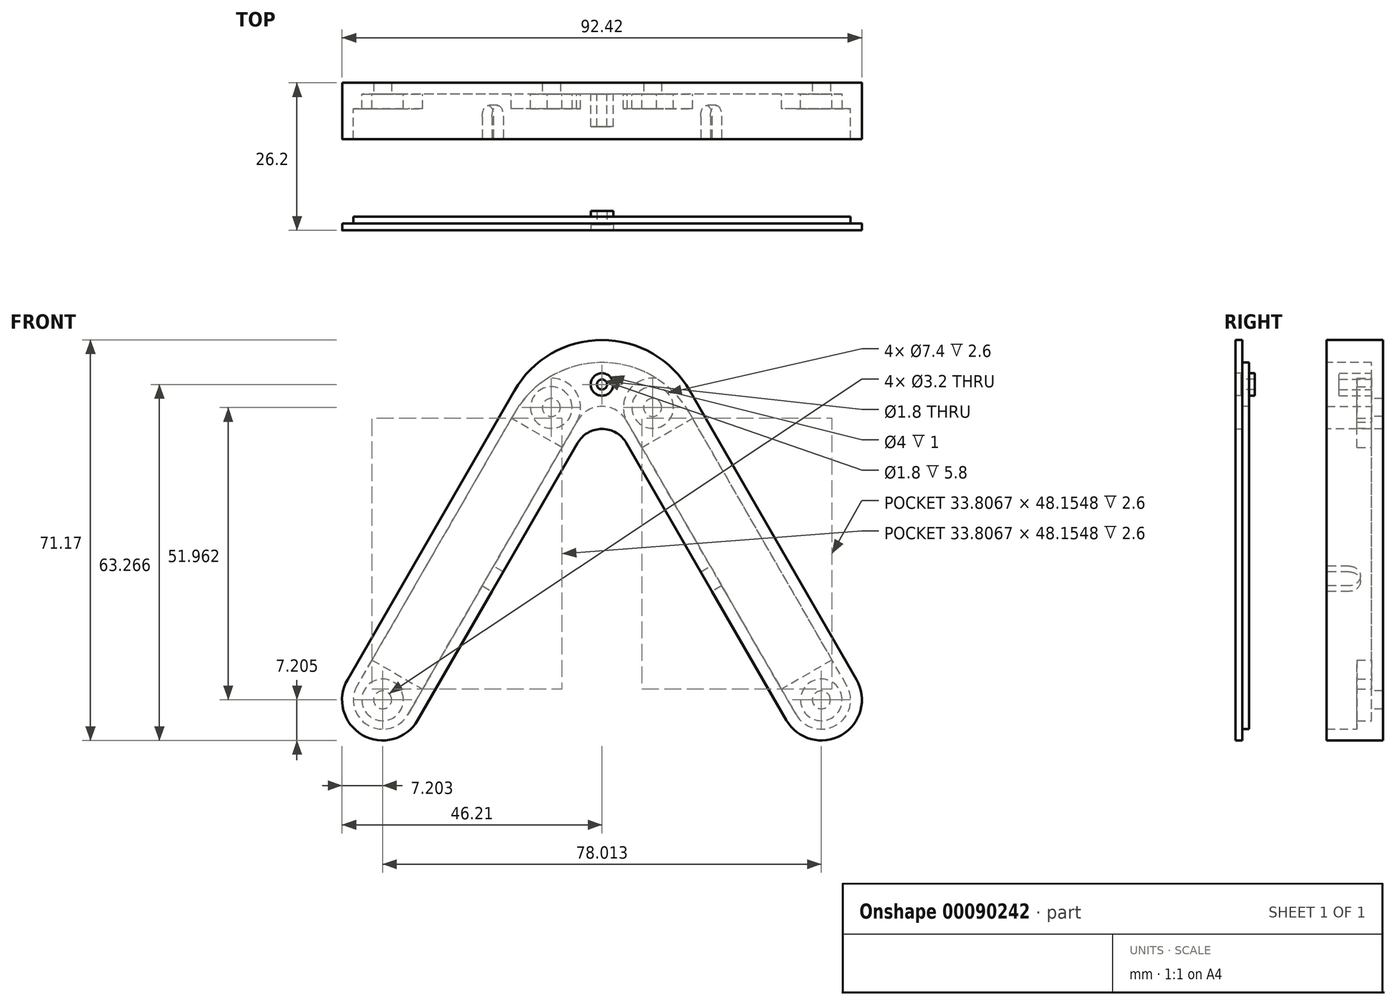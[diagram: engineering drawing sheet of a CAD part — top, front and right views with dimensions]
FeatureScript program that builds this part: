
annotation { "Feature Type Name" : "Feature", "Feature Type Description" : "" }
export const myFeature = defineFeature(function(context is Context, id is Id, definition is map)
    precondition{}
    {
        {
            var Q0;
            Q0=qCreatedBy(makeId("Front.planeOp"),FACE);
            var sketch = newSketch(context, id + "F0", { "sketchPlane" : qUnion([Q0])});
            skLineSegment(sketch, "E0", {"start": v(0, 45.47) * mm, "end": v(-52.5, -45.47) * mm});
            skLineSegment(sketch, "E1", {"start": v(-52.5, -45.47) * mm, "end": v(-35.87, -45.47) * mm});
            skLineSegment(sketch, "E2", {"start": v(52.5, -45.47) * mm, "end": v(0, 45.47) * mm});
            skLineSegment(sketch, "E3.0", {"start": v(35.87, -45.47) * mm, "end": v(0, 16.67) * mm});
            skLineSegment(sketch, "E3.2", {"start": v(0, 16.67) * mm, "end": v(-35.87, -45.47) * mm});
            skLineSegment(sketch, "E4.trimOffspring", {"start": v(35.87, -45.47) * mm, "end": v(52.5, -45.47) * mm});
            skSolve(sketch);
        }
        {
            var Q0;
            Q0 = qSketchRegion(id + "F0", true);
            extrude(context, id + "F1", {"entities" : qUnion([Q0]), "depth" : 2 * mm});
        }
        {
            var Q0;
            Q0=makeQuery(id+"F1.opExtrude","CAP_FACE",FACE,{"disambiguationData":[OSD([sQuery(id+"F0.wireOp",EDGE,"E0"),sQuery(id+"F0.wireOp",EDGE,"E1"),sQuery(id+"F0.wireOp",EDGE,"E2"),sQuery(id+"F0.wireOp",EDGE,"E3.0"),sQuery(id+"F0.wireOp",EDGE,"E3.2"),sQuery(id+"F0.wireOp",EDGE,"E4.trimOffspring")])],"isStart":false});
            var sketch = newSketch(context, id + "F2", { "sketchPlane" : qUnion([Q0])});
            skLineSegment(sketch, "E5.0", {"start": v(0, 16.67) * mm, "end": v(-35.87, -45.47) * mm});
            skLineSegment(sketch, "E5.1", {"start": v(0, 45.47) * mm, "end": v(-52.5, -45.47) * mm});
            skLineSegment(sketch, "E5.2", {"start": v(-52.5, -45.47) * mm, "end": v(-35.87, -45.47) * mm});
            skLineSegment(sketch, "E5.3", {"start": v(35.87, -45.47) * mm, "end": v(0, 16.67) * mm});
            skLineSegment(sketch, "E5.4", {"start": v(35.87, -45.47) * mm, "end": v(52.5, -45.47) * mm});
            skLineSegment(sketch, "E5.5", {"start": v(52.5, -45.47) * mm, "end": v(0, 45.47) * mm});
            skLineSegment(sketch, "E6.0", {"start": v(37.03, -43.47) * mm, "end": v(0, 20.67) * mm});
            skLineSegment(sketch, "E6.1", {"start": v(-49.04, -43.47) * mm, "end": v(-37.03, -43.47) * mm});
            skLineSegment(sketch, "E6.2", {"start": v(0, 41.47) * mm, "end": v(-49.04, -43.47) * mm});
            skLineSegment(sketch, "E6.3", {"start": v(0, 20.67) * mm, "end": v(-37.03, -43.47) * mm});
            skLineSegment(sketch, "E6.4", {"start": v(49.04, -43.47) * mm, "end": v(0, 41.47) * mm});
            skLineSegment(sketch, "E6.5", {"start": v(37.03, -43.47) * mm, "end": v(49.04, -43.47) * mm});
            skSolve(sketch);
        }
        {
            var Q0;
            Q0 = qSketchRegion(id + "F2", true);
            extrude(context, id + "F3", {"entities" : qUnion([Q0]), "operationType" : NewBodyOperationType.ADD, "depth" : 8 * mm});
        }
        {
            var Q0;
            Q0=makeQuery(id+"F1.opExtrude","CAP_FACE",FACE,{"disambiguationData":[OSD([sQuery(id+"F0.wireOp",EDGE,"E0"),sQuery(id+"F0.wireOp",EDGE,"E1"),sQuery(id+"F0.wireOp",EDGE,"E2"),sQuery(id+"F0.wireOp",EDGE,"E3.0"),sQuery(id+"F0.wireOp",EDGE,"E3.2"),sQuery(id+"F0.wireOp",EDGE,"E4.trimOffspring")])],"isStart":false});
            var sketch = newSketch(context, id + "F4", { "sketchPlane" : qUnion([Q0])});
            skLineSegment(sketch, "E7", {"start": v(-43.03, -43.47) * mm, "end": v(0, 31.07) * mm, "construction": true});
            skLineSegment(sketch, "E8", {"start": v(0, 41.47) * mm, "end": v(0, 0) * mm, "construction": true});
            skArc(sketch, "E9", {"start": v(-43.5, -33.9) * mm, "mid": v(-41.6, -41) * mm, "end": v(-34.5, -39.1) * mm});
            skCircle(sketch, "E10", {"center": v(-39, -36.5) * mm, "radius": 3.7 * mm});
            skCircle(sketch, "E11", {"center": v(-9, 15.47) * mm, "radius": 3.7 * mm});
            skArc(sketch, "E12", {"start": v(-4.5, 12.87) * mm, "mid": v(-6.4, 19.97) * mm, "end": v(-13.5, 18.07) * mm});
            skLineSegment(sketch, "E13", {"start": v(12, 20.67) * mm, "end": v(-12, 20.67) * mm, "construction": true});
            skLineSegment(sketch, "E14", {"start": v(-13.5, 18.07) * mm, "end": v(-4.5, 12.87) * mm, "construction": true});
            skLineSegment(sketch, "E15", {"start": v(-4.5, 12.87) * mm, "end": v(-7.1, 8.36) * mm});
            skLineSegment(sketch, "E16", {"start": v(-7.1, 8.36) * mm, "end": v(-16.1, 13.56) * mm});
            skLineSegment(sketch, "E17", {"start": v(-16.1, 13.56) * mm, "end": v(-13.5, 18.07) * mm});
            skLineSegment(sketch, "E18", {"start": v(-34.5, -39.1) * mm, "end": v(-43.5, -33.9) * mm, "construction": true});
            skLineSegment(sketch, "E19", {"start": v(-43.5, -33.9) * mm, "end": v(-40.9, -29.4) * mm});
            skLineSegment(sketch, "E20", {"start": v(-40.9, -29.4) * mm, "end": v(-31.9, -34.6) * mm});
            skLineSegment(sketch, "E21", {"start": v(-31.9, -34.6) * mm, "end": v(-34.5, -39.1) * mm});
            skLineSegment(sketch, "E22.MirrorCS", {"start": v(40.9, -29.4) * mm, "end": v(31.9, -34.6) * mm});
            skLineSegment(sketch, "E23.MirrorCS", {"start": v(31.9, -34.6) * mm, "end": v(34.5, -39.1) * mm});
            skLineSegment(sketch, "E24.MirrorCS", {"start": v(43.5, -33.9) * mm, "end": v(40.9, -29.4) * mm});
            skArc(sketch, "E25.MirrorCS", {"start": v(43.5, -33.9) * mm, "mid": v(41.6, -41) * mm, "end": v(34.5, -39.1) * mm});
            skArc(sketch, "E26.MirrorCS", {"start": v(4.5, 12.87) * mm, "mid": v(6.4, 19.97) * mm, "end": v(13.5, 18.07) * mm});
            skLineSegment(sketch, "E27.MirrorCS", {"start": v(7.1, 8.36) * mm, "end": v(16.1, 13.56) * mm});
            skLineSegment(sketch, "E28.MirrorCS", {"start": v(4.5, 12.87) * mm, "end": v(7.1, 8.36) * mm});
            skCircle(sketch, "E29.MirrorC", {"center": v(9, 15.47) * mm, "radius": 3.7 * mm});
            skCircle(sketch, "E30.MirrorC", {"center": v(39, -36.5) * mm, "radius": 3.7 * mm});
            skLineSegment(sketch, "E31.MirrorCS", {"start": v(34.5, -39.1) * mm, "end": v(43.5, -33.9) * mm, "construction": true});
            skLineSegment(sketch, "E32.MirrorCS", {"start": v(13.5, 18.07) * mm, "end": v(4.5, 12.87) * mm, "construction": true});
            skLineSegment(sketch, "E33.MirrorCS", {"start": v(16.1, 13.56) * mm, "end": v(13.5, 18.07) * mm});
            skSolve(sketch);
        }
        {
            var Q0;
            Q0 = qSketchRegion(id + "F4", true);
            extrude(context, id + "F5", {"entities" : qUnion([Q0]), "operationType" : NewBodyOperationType.ADD, "depth" : 2.6 * mm});
        }
        {
            var Q0;
            Q0=makeQuery(id+"F5.boolean.opBoolean","SPLIT",FACE,{"disambiguationData":[TD([makeQuery(id+"F5.opExtrude","SWEPT_FACE",FACE,{"disambiguationData":[OSD([sQuery(id+"F4.wireOp",EDGE,"E16")])]})])],"derivedFrom":makeQuery(id+"F1.opExtrude","CAP_FACE",FACE,{"disambiguationData":[OSD([sQuery(id+"F0.wireOp",EDGE,"E0"),sQuery(id+"F0.wireOp",EDGE,"E1"),sQuery(id+"F0.wireOp",EDGE,"E2"),sQuery(id+"F0.wireOp",EDGE,"E3.0"),sQuery(id+"F0.wireOp",EDGE,"E3.2"),sQuery(id+"F0.wireOp",EDGE,"E4.trimOffspring")])],"isStart":false})});
            var sketch = newSketch(context, id + "F6", { "sketchPlane" : qUnion([Q0])});
            skArc(sketch, "E34.0", {"start": v(-43.5, -33.9) * mm, "mid": v(-41.6, -41) * mm, "end": v(-34.5, -39.1) * mm});
            skArc(sketch, "E34.1", {"start": v(43.5, -33.9) * mm, "mid": v(41.6, -41) * mm, "end": v(34.5, -39.1) * mm});
            skArc(sketch, "E35.0", {"start": v(-45.24, -32.9) * mm, "mid": v(-42.6, -42.73) * mm, "end": v(-32.77, -40.1) * mm});
            skArc(sketch, "E36.0", {"start": v(45.24, -32.9) * mm, "mid": v(42.6, -42.73) * mm, "end": v(32.77, -40.1) * mm});
            skLineSegment(sketch, "E37", {"start": v(32.77, -40.1) * mm, "end": v(34.5, -39.1) * mm});
            skLineSegment(sketch, "E38", {"start": v(43.5, -33.9) * mm, "end": v(45.24, -32.9) * mm});
            skLineSegment(sketch, "E39", {"start": v(-32.77, -40.1) * mm, "end": v(-34.5, -39.1) * mm});
            skLineSegment(sketch, "E40", {"start": v(-43.5, -33.9) * mm, "end": v(-45.24, -32.9) * mm});
            skSolve(sketch);
        }
        {
            var Q0;
            Q0 = qSketchRegion(id + "F6", true);
            var Q1;
            Q1=makeQuery(id+"F3.opExtrude","CAP_FACE",FACE,{"disambiguationData":[OSD([sQuery(id+"F2.wireOp",EDGE,"E5.0"),sQuery(id+"F2.wireOp",EDGE,"E5.1"),sQuery(id+"F2.wireOp",EDGE,"E5.2"),sQuery(id+"F2.wireOp",EDGE,"E5.3"),sQuery(id+"F2.wireOp",EDGE,"E5.4"),sQuery(id+"F2.wireOp",EDGE,"E5.5"),sQuery(id+"F2.wireOp",EDGE,"E6.0"),sQuery(id+"F2.wireOp",EDGE,"E6.1"),sQuery(id+"F2.wireOp",EDGE,"E6.2"),sQuery(id+"F2.wireOp",EDGE,"E6.3"),sQuery(id+"F2.wireOp",EDGE,"E6.4"),sQuery(id+"F2.wireOp",EDGE,"E6.5")])],"isStart":false});
            extrude(context, id + "F7", {"entities" : qUnion([Q0]), "operationType" : NewBodyOperationType.ADD, "endBound" : BoundingType.UP_TO_SURFACE, "endBoundEntityFace" : qUnion([Q1]), "depth" : 25 * mm});
        }
        {
            var Q0;
            {var subQ0=sQuery(id+"F2.wireOp",EDGE,"E6.5");var subQ1=sQuery(id+"F2.wireOp",EDGE,"E6.4");var subQ2=sQuery(id+"F2.wireOp",EDGE,"E6.3");var subQ3=sQuery(id+"F2.wireOp",EDGE,"E6.2");var subQ4=sQuery(id+"F2.wireOp",EDGE,"E6.1");var subQ5=sQuery(id+"F2.wireOp",EDGE,"E6.0");var subQ6=sQuery(id+"F2.wireOp",EDGE,"E5.5");var subQ7=sQuery(id+"F2.wireOp",EDGE,"E5.4");var subQ8=sQuery(id+"F2.wireOp",EDGE,"E5.3");var subQ9=sQuery(id+"F2.wireOp",EDGE,"E5.2");var subQ10=sQuery(id+"F2.wireOp",EDGE,"E5.1");var subQ11=sQuery(id+"F2.wireOp",EDGE,"E5.0");Q0=makeQuery(id+"F7.boolean.opBoolean","MERGE",FACE,{"derivedFrom":[makeQuery(id+"F3.opExtrude","CAP_FACE",FACE,{"disambiguationData":[OSD([subQ11,subQ10,subQ9,subQ8,subQ7,subQ6,subQ5,subQ4,subQ3,subQ2,subQ1,subQ0])],"isStart":false}),makeQuery(id+"F7.opExtrude","CAP_FACE",FACE,{"disambiguationData":[OSD([subQ11,subQ10,subQ9,subQ8,subQ7,subQ6,subQ5,subQ4,subQ3,subQ2,subQ1,subQ0]),ownerDisambiguation([makeQuery(id+"F7.opExtrude","SWEPT_BODY",BODY,{"disambiguationData":[OSD([sQuery(id+"F6.wireOp",EDGE,"E34.0"),sQuery(id+"F6.wireOp",EDGE,"E35.0"),sQuery(id+"F6.wireOp",EDGE,"E39"),sQuery(id+"F6.wireOp",EDGE,"E40")])]})])],"isStart":false}),makeQuery(id+"F7.opExtrude","CAP_FACE",FACE,{"disambiguationData":[OSD([subQ11,subQ10,subQ9,subQ8,subQ7,subQ6,subQ5,subQ4,subQ3,subQ2,subQ1,subQ0]),ownerDisambiguation([makeQuery(id+"F7.opExtrude","SWEPT_BODY",BODY,{"disambiguationData":[OSD([sQuery(id+"F6.wireOp",EDGE,"E34.1"),sQuery(id+"F6.wireOp",EDGE,"E36.0"),sQuery(id+"F6.wireOp",EDGE,"E37"),sQuery(id+"F6.wireOp",EDGE,"E38")])]})])],"isStart":false})]});}
            var sketch = newSketch(context, id + "F8", { "sketchPlane" : qUnion([Q0])});
            skArc(sketch, "E41.0", {"start": v(-45.24, -32.9) * mm, "mid": v(-42.6, -42.73) * mm, "end": v(-32.77, -40.1) * mm});
            skArc(sketch, "E41.1", {"start": v(45.24, -32.9) * mm, "mid": v(42.6, -42.73) * mm, "end": v(32.77, -40.1) * mm});
            skLineSegment(sketch, "E42", {"start": v(-32.77, -40.1) * mm, "end": v(-35.87, -45.47) * mm});
            skLineSegment(sketch, "E43", {"start": v(-35.87, -45.47) * mm, "end": v(-52.5, -45.47) * mm});
            skLineSegment(sketch, "E44", {"start": v(-52.5, -45.47) * mm, "end": v(-45.24, -32.9) * mm});
            skLineSegment(sketch, "E45", {"start": v(32.77, -40.1) * mm, "end": v(35.87, -45.47) * mm});
            skLineSegment(sketch, "E46", {"start": v(35.87, -45.47) * mm, "end": v(52.5, -45.47) * mm});
            skLineSegment(sketch, "E47", {"start": v(52.5, -45.47) * mm, "end": v(45.24, -32.9) * mm});
            skSolve(sketch);
        }
        {
            var Q0;
            Q0 = qSketchRegion(id + "F8", true);
            extrude(context, id + "F9", {"entities" : qUnion([Q0]), "operationType" : NewBodyOperationType.REMOVE, "endBound" : BoundingType.THROUGH_ALL, "oppositeDirection" : true, "depth" : 25 * mm});
        }
        {
            var Q0;
            Q0=makeQuery(id+"F3.opExtrude","SWEPT_EDGE",EDGE,{"disambiguationData":[OSD([sQuery(id+"F2.wireOp",EDGE,"E6.2"),sQuery(id+"F2.wireOp",EDGE,"E6.4")])]});
            var Q1;
            Q1=makeQuery(id+"F3.boolean.opBoolean","MERGE",EDGE,{"derivedFrom":[makeQuery(id+"F1.opExtrude","SWEPT_EDGE",EDGE,{"disambiguationData":[OSD([sQuery(id+"F0.wireOp",EDGE,"E0"),sQuery(id+"F0.wireOp",EDGE,"E2")])]}),makeQuery(id+"F3.opExtrude","SWEPT_EDGE",EDGE,{"disambiguationData":[OSD([sQuery(id+"F2.wireOp",EDGE,"E5.1"),sQuery(id+"F2.wireOp",EDGE,"E5.5")])]})]});
            fillet(context, id + "F10", {"entities" : qUnion([Q0, Q1]), "radius" : 18 * mm, "tangentPropagation" : true, "allowEdgeOverflow" : false});
        }
        {
            var Q0;
            Q0=makeQuery(id+"F3.boolean.opBoolean","MERGE",EDGE,{"derivedFrom":[makeQuery(id+"F1.opExtrude","SWEPT_EDGE",EDGE,{"disambiguationData":[OSD([sQuery(id+"F0.wireOp",EDGE,"E3.0"),sQuery(id+"F0.wireOp",EDGE,"E3.2")])]}),makeQuery(id+"F3.opExtrude","SWEPT_EDGE",EDGE,{"disambiguationData":[OSD([sQuery(id+"F2.wireOp",EDGE,"E5.0"),sQuery(id+"F2.wireOp",EDGE,"E5.3")])]})]});
            var Q1;
            Q1=makeQuery(id+"F3.opExtrude","SWEPT_EDGE",EDGE,{"disambiguationData":[OSD([sQuery(id+"F2.wireOp",EDGE,"E6.0"),sQuery(id+"F2.wireOp",EDGE,"E6.3")])]});
            fillet(context, id + "F11", {"entities" : qUnion([Q0, Q1]), "radius" : 5 * mm, "tangentPropagation" : true, "allowEdgeOverflow" : false});
        }
        {
            var Q0;
            Q0=makeQuery(id+"F5.boolean.opBoolean","SPLIT",FACE,{"disambiguationData":[TD([makeQuery(id+"F5.opExtrude","SWEPT_FACE",FACE,{"disambiguationData":[OSD([sQuery(id+"F4.wireOp",EDGE,"E30.MirrorC")])]})])],"derivedFrom":makeQuery(id+"F1.opExtrude","CAP_FACE",FACE,{"disambiguationData":[OSD([sQuery(id+"F0.wireOp",EDGE,"E0"),sQuery(id+"F0.wireOp",EDGE,"E1"),sQuery(id+"F0.wireOp",EDGE,"E2"),sQuery(id+"F0.wireOp",EDGE,"E3.0"),sQuery(id+"F0.wireOp",EDGE,"E3.2"),sQuery(id+"F0.wireOp",EDGE,"E4.trimOffspring")])],"isStart":false})});
            var sketch = newSketch(context, id + "F12", { "sketchPlane" : qUnion([Q0])});
            skCircle(sketch, "E48", {"center": v(-9, 15.47) * mm, "radius": 1.6 * mm});
            skCircle(sketch, "E49", {"center": v(9, 15.47) * mm, "radius": 1.6 * mm});
            skCircle(sketch, "E50", {"center": v(-39, -36.5) * mm, "radius": 1.6 * mm});
            skCircle(sketch, "E51", {"center": v(39, -36.5) * mm, "radius": 1.6 * mm});
            skSolve(sketch);
        }
        {
            var Q0;
            Q0 = qSketchRegion(id + "F12", true);
            extrude(context, id + "F13", {"entities" : qUnion([Q0]), "operationType" : NewBodyOperationType.REMOVE, "endBound" : BoundingType.THROUGH_ALL, "oppositeDirection" : true, "depth" : 25 * mm});
        }
        {
            var Q0;
            {var subQ0=sQuery(id+"F2.wireOp",EDGE,"E6.5");var subQ1=sQuery(id+"F2.wireOp",EDGE,"E6.4");var subQ2=sQuery(id+"F2.wireOp",EDGE,"E6.3");var subQ3=sQuery(id+"F2.wireOp",EDGE,"E6.2");var subQ4=sQuery(id+"F2.wireOp",EDGE,"E6.1");var subQ5=sQuery(id+"F2.wireOp",EDGE,"E6.0");var subQ6=sQuery(id+"F2.wireOp",EDGE,"E5.5");var subQ7=sQuery(id+"F2.wireOp",EDGE,"E5.4");var subQ8=sQuery(id+"F2.wireOp",EDGE,"E5.3");var subQ9=sQuery(id+"F2.wireOp",EDGE,"E5.2");var subQ10=sQuery(id+"F2.wireOp",EDGE,"E5.1");var subQ11=sQuery(id+"F2.wireOp",EDGE,"E5.0");Q0=makeQuery(id+"F7.boolean.opBoolean","MERGE",FACE,{"derivedFrom":[makeQuery(id+"F3.opExtrude","CAP_FACE",FACE,{"disambiguationData":[OSD([subQ11,subQ10,subQ9,subQ8,subQ7,subQ6,subQ5,subQ4,subQ3,subQ2,subQ1,subQ0])],"isStart":false}),makeQuery(id+"F7.opExtrude","CAP_FACE",FACE,{"disambiguationData":[OSD([subQ11,subQ10,subQ9,subQ8,subQ7,subQ6,subQ5,subQ4,subQ3,subQ2,subQ1,subQ0]),ownerDisambiguation([makeQuery(id+"F7.opExtrude","SWEPT_BODY",BODY,{"disambiguationData":[OSD([sQuery(id+"F6.wireOp",EDGE,"E34.0"),sQuery(id+"F6.wireOp",EDGE,"E35.0"),sQuery(id+"F6.wireOp",EDGE,"E39"),sQuery(id+"F6.wireOp",EDGE,"E40")])]})])],"isStart":false}),makeQuery(id+"F7.opExtrude","CAP_FACE",FACE,{"disambiguationData":[OSD([subQ11,subQ10,subQ9,subQ8,subQ7,subQ6,subQ5,subQ4,subQ3,subQ2,subQ1,subQ0]),ownerDisambiguation([makeQuery(id+"F7.opExtrude","SWEPT_BODY",BODY,{"disambiguationData":[OSD([sQuery(id+"F6.wireOp",EDGE,"E34.1"),sQuery(id+"F6.wireOp",EDGE,"E36.0"),sQuery(id+"F6.wireOp",EDGE,"E37"),sQuery(id+"F6.wireOp",EDGE,"E38")])]})])],"isStart":false})]});}
            var sketch = newSketch(context, id + "F14", { "sketchPlane" : qUnion([Q0])});
            skLineSegment(sketch, "E52.0", {"start": v(-4.33, 13.17) * mm, "end": v(-34.5, -39.1) * mm, "construction": true});
            skLineSegment(sketch, "E52.1", {"start": v(-4.33, 9.17) * mm, "end": v(-32.77, -40.1) * mm, "construction": true});
            skPoint(sketch, "E53", {"position": v(-18.55, -15.46) * mm});
            skLineSegment(sketch, "E54", {"start": v(-19.55, -17.2) * mm, "end": v(-17.55, -13.73) * mm});
            skLineSegment(sketch, "E55", {"start": v(-17.55, -13.73) * mm, "end": v(-19.28, -12.73) * mm});
            skLineSegment(sketch, "E56", {"start": v(-19.28, -12.73) * mm, "end": v(-21.28, -16.2) * mm});
            skLineSegment(sketch, "E57", {"start": v(-21.28, -16.2) * mm, "end": v(-19.55, -17.2) * mm});
            skLineSegment(sketch, "E58.MirrorCS", {"start": v(21.28, -16.2) * mm, "end": v(19.55, -17.2) * mm});
            skLineSegment(sketch, "E59.MirrorCS", {"start": v(17.55, -13.73) * mm, "end": v(19.28, -12.73) * mm});
            skLineSegment(sketch, "E60.MirrorCS", {"start": v(19.28, -12.73) * mm, "end": v(21.28, -16.2) * mm});
            skLineSegment(sketch, "E61.MirrorCS", {"start": v(4.33, 13.17) * mm, "end": v(34.5, -39.1) * mm, "construction": true});
            skLineSegment(sketch, "E62.MirrorCS", {"start": v(4.33, 9.17) * mm, "end": v(32.77, -40.1) * mm, "construction": true});
            skLineSegment(sketch, "E63.MirrorCS", {"start": v(19.55, -17.2) * mm, "end": v(17.55, -13.73) * mm});
            skPoint(sketch, "E64.MirrorP", {"position": v(18.55, -15.46) * mm});
            skSolve(sketch);
        }
        {
            var Q0;
            Q0 = qSketchRegion(id + "F14", true);
            extrude(context, id + "F15", {"entities" : qUnion([Q0]), "operationType" : NewBodyOperationType.REMOVE, "oppositeDirection" : true, "depth" : 6 * mm});
        }
        {
            var Q0;
            Q0=makeQuery(id+"F15.boolean.opBoolean","COPY",EDGE,{"derivedFrom":makeQuery(id+"F15.opExtrude","CAP_EDGE",EDGE,{"disambiguationData":[OSD([sQuery(id+"F14.wireOp",EDGE,"E55")])],"isStart":false})});
            var Q1;
            Q1=makeQuery(id+"F15.boolean.opBoolean","COPY",EDGE,{"derivedFrom":makeQuery(id+"F15.opExtrude","CAP_EDGE",EDGE,{"disambiguationData":[OSD([sQuery(id+"F14.wireOp",EDGE,"E59.MirrorCS")])],"isStart":false})});
            var Q2;
            Q2=makeQuery(id+"F15.boolean.opBoolean","COPY",EDGE,{"derivedFrom":makeQuery(id+"F15.opExtrude","CAP_EDGE",EDGE,{"disambiguationData":[OSD([sQuery(id+"F14.wireOp",EDGE,"E58.MirrorCS")])],"isStart":false})});
            var Q3;
            Q3=makeQuery(id+"F15.boolean.opBoolean","COPY",EDGE,{"derivedFrom":makeQuery(id+"F15.opExtrude","CAP_EDGE",EDGE,{"disambiguationData":[OSD([sQuery(id+"F14.wireOp",EDGE,"E57")])],"isStart":false})});
            fillet(context, id + "F16", {"entities" : qUnion([Q0, Q1, Q2, Q3]), "radius" : 2 * mm, "tangentPropagation" : true, "allowEdgeOverflow" : false});
        }
        {
            var Q0;
            Q0=makeQuery(id+"F5.boolean.opBoolean","SPLIT",FACE,{"disambiguationData":[TD([makeQuery(id+"F5.opExtrude","SWEPT_FACE",FACE,{"disambiguationData":[OSD([sQuery(id+"F4.wireOp",EDGE,"E12")])]})])],"derivedFrom":makeQuery(id+"F1.opExtrude","CAP_FACE",FACE,{"disambiguationData":[OSD([sQuery(id+"F0.wireOp",EDGE,"E0"),sQuery(id+"F0.wireOp",EDGE,"E1"),sQuery(id+"F0.wireOp",EDGE,"E2"),sQuery(id+"F0.wireOp",EDGE,"E3.0"),sQuery(id+"F0.wireOp",EDGE,"E3.2"),sQuery(id+"F0.wireOp",EDGE,"E4.trimOffspring")])],"isStart":false})});
            var sketch = newSketch(context, id + "F17", { "sketchPlane" : qUnion([Q0])});
            skLineSegment(sketch, "E65", {"start": v(0, 15.67) * mm, "end": v(0, 23.47) * mm, "construction": true});
            skCircle(sketch, "E66", {"center": v(0, 19.57) * mm, "radius": 2 * mm});
            skCircle(sketch, "E67", {"center": v(0, 19.57) * mm, "radius": 0.9 * mm});
            skSolve(sketch);
        }
        {
            var Q0;
            Q0 = qSketchRegion(id + "F17", true);
            extrude(context, id + "F18", {"entities" : qUnion([Q0]), "operationType" : NewBodyOperationType.ADD, "depth" : 5.8 * mm});
        }
        {
            var Q0;
            {var subQ0=sQuery(id+"F2.wireOp",EDGE,"E6.2");var subQ1=sQuery(id+"F2.wireOp",EDGE,"E6.0");var subQ2=sQuery(id+"F2.wireOp",EDGE,"E5.5");var subQ3=sQuery(id+"F0.wireOp",EDGE,"E0");var subQ4=sQuery(id+"F2.wireOp",EDGE,"E5.0");var subQ5=sQuery(id+"F2.wireOp",EDGE,"E5.3");var subQ6=sQuery(id+"F2.wireOp",EDGE,"E5.1");var subQ8=sQuery(id+"F6.wireOp",EDGE,"E34.1");var subQ9=sQuery(id+"F2.wireOp",EDGE,"E6.3");var subQ10=sQuery(id+"F6.wireOp",EDGE,"E36.0");var subQ11=sQuery(id+"F2.wireOp",EDGE,"E6.4");var subQ12=sQuery(id+"F6.wireOp",EDGE,"E34.0");var subQ13=sQuery(id+"F6.wireOp",EDGE,"E35.0");var subQ14=sQuery(id+"F2.wireOp",EDGE,"E6.5");var subQ15=sQuery(id+"F2.wireOp",EDGE,"E6.1");var subQ16=sQuery(id+"F2.wireOp",EDGE,"E5.4");var subQ17=sQuery(id+"F2.wireOp",EDGE,"E5.2");Q0=makeQuery(id+"F15.boolean.opBoolean","SPLIT",FACE,{"disambiguationData":[TD([makeQuery(id+"F1.opExtrude","SWEPT_FACE",FACE,{"disambiguationData":[OSD([subQ3])]})])],"derivedFrom":makeQuery(id+"F7.boolean.opBoolean","MERGE",FACE,{"derivedFrom":[makeQuery(id+"F3.opExtrude","CAP_FACE",FACE,{"disambiguationData":[OSD([subQ4,subQ6,subQ17,subQ5,subQ16,subQ2,subQ1,subQ15,subQ0,subQ9,subQ11,subQ14])],"isStart":false}),makeQuery(id+"F7.opExtrude","CAP_FACE",FACE,{"disambiguationData":[OSD([subQ4,subQ6,subQ17,subQ5,subQ16,subQ2,subQ1,subQ15,subQ0,subQ9,subQ11,subQ14]),ownerDisambiguation([makeQuery(id+"F7.opExtrude","SWEPT_BODY",BODY,{"disambiguationData":[OSD([subQ12,subQ13,sQuery(id+"F6.wireOp",EDGE,"E39"),sQuery(id+"F6.wireOp",EDGE,"E40")])]})])],"isStart":false}),makeQuery(id+"F7.opExtrude","CAP_FACE",FACE,{"disambiguationData":[OSD([subQ4,subQ6,subQ17,subQ5,subQ16,subQ2,subQ1,subQ15,subQ0,subQ9,subQ11,subQ14]),ownerDisambiguation([makeQuery(id+"F7.opExtrude","SWEPT_BODY",BODY,{"disambiguationData":[OSD([subQ8,subQ10,sQuery(id+"F6.wireOp",EDGE,"E37"),sQuery(id+"F6.wireOp",EDGE,"E38")])]})])],"isStart":false})]})});}
            cPlane(context, id + "F19", {"entities" : qUnion([Q0]), "cplaneType" : CPlaneType.OFFSET, "offset" : 15 * mm, "width" : 150 * mm, "height" : 150 * mm});
        }
        {
            var Q0;
            Q0=qCreatedBy(id+"F19.planeOp",FACE);
            var sketch = newSketch(context, id + "F20", { "sketchPlane" : qUnion([Q0])});
            skArc(sketch, "E68.0", {"start": v(15.59, 18.47) * mm, "mid": v(0, 27.47) * mm, "end": v(-15.59, 18.47) * mm});
            skLineSegment(sketch, "E68.1", {"start": v(45.24, -32.9) * mm, "end": v(15.59, 18.47) * mm});
            skArc(sketch, "E68.2", {"start": v(45.24, -32.9) * mm, "mid": v(42.6, -42.73) * mm, "end": v(32.77, -40.1) * mm});
            skArc(sketch, "E68.3", {"start": v(-4.33, 9.17) * mm, "mid": v(0, 11.67) * mm, "end": v(4.33, 9.17) * mm});
            skArc(sketch, "E68.4", {"start": v(-45.24, -32.9) * mm, "mid": v(-42.6, -42.73) * mm, "end": v(-32.77, -40.1) * mm});
            skLineSegment(sketch, "E68.5", {"start": v(-15.59, 18.47) * mm, "end": v(-45.24, -32.9) * mm});
            skLineSegment(sketch, "E69", {"start": v(-4.33, 9.17) * mm, "end": v(-32.77, -40.1) * mm});
            skLineSegment(sketch, "E70", {"start": v(4.33, 9.17) * mm, "end": v(32.77, -40.1) * mm});
            skSolve(sketch);
        }
        {
            var Q0;
            Q0 = qSketchRegion(id + "F20", true);
            extrude(context, id + "F21", {"entities" : qUnion([Q0]), "depth" : 1.2 * mm});
        }
        {
            var Q0;
            Q0=makeQuery(id+"F21.opExtrude","CAP_FACE",FACE,{"disambiguationData":[OSD([sQuery(id+"F20.wireOp",EDGE,"E68.0"),sQuery(id+"F20.wireOp",EDGE,"E68.1"),sQuery(id+"F20.wireOp",EDGE,"E68.2"),sQuery(id+"F20.wireOp",EDGE,"E68.3"),sQuery(id+"F20.wireOp",EDGE,"E68.4"),sQuery(id+"F20.wireOp",EDGE,"E68.5"),sQuery(id+"F20.wireOp",EDGE,"E69"),sQuery(id+"F20.wireOp",EDGE,"E70")])],"isStart":true});
            var sketch = newSketch(context, id + "F22", { "sketchPlane" : qUnion([Q0])});
            skArc(sketch, "E71.0", {"start": v(-4.33, 13.17) * mm, "mid": v(0, 15.67) * mm, "end": v(4.33, 13.17) * mm});
            skArc(sketch, "E71.1", {"start": v(-43.5, -33.9) * mm, "mid": v(-41.6, -41) * mm, "end": v(-34.5, -39.1) * mm});
            skLineSegment(sketch, "E71.2", {"start": v(-43.5, -33.9) * mm, "end": v(-15.59, 14.47) * mm});
            skArc(sketch, "E71.3", {"start": v(15.59, 14.47) * mm, "mid": v(0, 23.47) * mm, "end": v(-15.59, 14.47) * mm});
            skLineSegment(sketch, "E71.4", {"start": v(15.59, 14.47) * mm, "end": v(43.5, -33.9) * mm});
            skArc(sketch, "E71.5", {"start": v(43.5, -33.9) * mm, "mid": v(41.6, -41) * mm, "end": v(34.5, -39.1) * mm});
            skLineSegment(sketch, "E72", {"start": v(-4.33, 13.17) * mm, "end": v(-34.5, -39.1) * mm});
            skLineSegment(sketch, "E73", {"start": v(34.5, -39.1) * mm, "end": v(4.33, 13.17) * mm});
            skSolve(sketch);
        }
        {
            var Q0;
            Q0 = qSketchRegion(id + "F22", true);
            extrude(context, id + "F23", {"entities" : qUnion([Q0]), "operationType" : NewBodyOperationType.ADD, "depth" : 1.2 * mm});
        }
        {
            var Q0;
            Q0=makeQuery(id+"F21.opExtrude","CAP_FACE",FACE,{"disambiguationData":[OSD([sQuery(id+"F20.wireOp",EDGE,"E68.0"),sQuery(id+"F20.wireOp",EDGE,"E68.1"),sQuery(id+"F20.wireOp",EDGE,"E68.2"),sQuery(id+"F20.wireOp",EDGE,"E68.3"),sQuery(id+"F20.wireOp",EDGE,"E68.4"),sQuery(id+"F20.wireOp",EDGE,"E68.5"),sQuery(id+"F20.wireOp",EDGE,"E69"),sQuery(id+"F20.wireOp",EDGE,"E70")])],"isStart":false});
            var sketch = newSketch(context, id + "F24", { "sketchPlane" : qUnion([Q0])});
            skCircle(sketch, "E74.0", {"center": v(0, 19.57) * mm, "radius": 2 * mm});
            skSolve(sketch);
        }
        {
            var Q0;
            Q0 = qSketchRegion(id + "F24", true);
            extrude(context, id + "F25", {"entities" : qUnion([Q0]), "operationType" : NewBodyOperationType.ADD, "oppositeDirection" : true, "depth" : 3.4 * mm});
        }
        {
            var Q0;
            Q0=sQuery(id+"F24.wireOp",VERTEX,"E74.0.center");
            var Q1;
            Q1=makeQuery(id+"F21.opExtrude","SWEPT_BODY",BODY,{"disambiguationData":[OSD([sQuery(id+"F20.wireOp",EDGE,"E68.0"),sQuery(id+"F20.wireOp",EDGE,"E68.1"),sQuery(id+"F20.wireOp",EDGE,"E68.2"),sQuery(id+"F20.wireOp",EDGE,"E68.3"),sQuery(id+"F20.wireOp",EDGE,"E68.4"),sQuery(id+"F20.wireOp",EDGE,"E68.5"),sQuery(id+"F20.wireOp",EDGE,"E69"),sQuery(id+"F20.wireOp",EDGE,"E70")])]});
            hole(context, id + "F26", {"style" : HoleStyle.C_BORE, "endStyle" : HoleEndStyle.THROUGH, "holeDiameter" : 1.8 * mm, "cBoreDiameter" : 4 * mm, "cBoreDepth" : 1 * mm, "locations" : qUnion([Q0]), "scope" : qUnion([Q1]), "isTappedThrough" : true});
        }
    });
